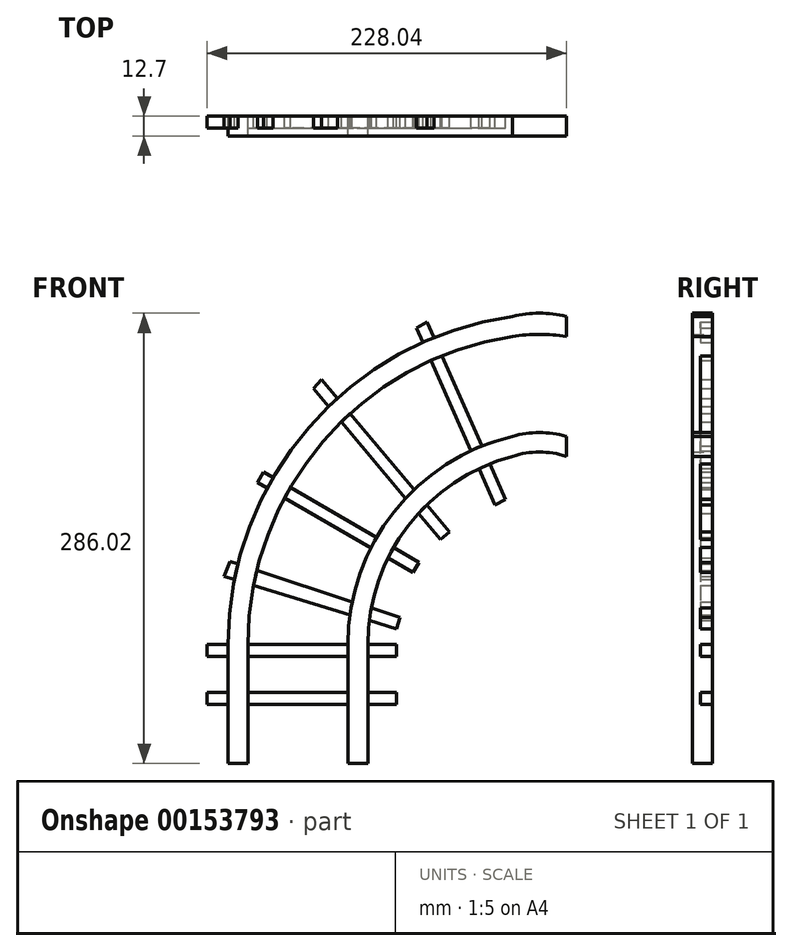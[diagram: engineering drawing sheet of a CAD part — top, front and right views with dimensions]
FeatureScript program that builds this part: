
annotation { "Feature Type Name" : "Feature", "Feature Type Description" : "" }
export const myFeature = defineFeature(function(context is Context, id is Id, definition is map)
    precondition{}
    {
        {
            var Q0;
            Q0=qCreatedBy(makeId("Front.planeOp"),FACE);
            var sketch = newSketch(context, id + "F0", { "sketchPlane" : qUnion([Q0])});
            skLineSegment(sketch, "E0", {"start": v(-58.28, 0) * mm, "end": v(-45.58, 0) * mm});
            skLineSegment(sketch, "E1", {"start": v(-45.58, 0) * mm, "end": v(-45.58, -75.5) * mm});
            skLineSegment(sketch, "E2", {"start": v(-45.58, -75.5) * mm, "end": v(-58.28, -75.5) * mm});
            skLineSegment(sketch, "E3", {"start": v(-58.28, -75.5) * mm, "end": v(-58.28, 0) * mm});
            skLineSegment(sketch, "E4", {"start": v(17.92, 0) * mm, "end": v(30.62, 0) * mm});
            skLineSegment(sketch, "E5", {"start": v(30.62, 0) * mm, "end": v(30.62, -75.5) * mm});
            skLineSegment(sketch, "E6", {"start": v(30.62, -75.5) * mm, "end": v(17.92, -75.5) * mm});
            skLineSegment(sketch, "E7", {"start": v(17.92, -75.5) * mm, "end": v(17.92, 0) * mm});
            skArc(sketch, "E8", {"start": v(122.47, 119.63) * mm, "mid": v(56.23, 75.41) * mm, "end": v(30.62, 0) * mm});
            skArc(sketch, "E9", {"start": v(122.47, 132.33) * mm, "mid": v(47.2, 84.32) * mm, "end": v(17.92, 0) * mm});
            skArc(sketch, "E10", {"start": v(122.47, 195.83) * mm, "mid": v(2.2, 129.03) * mm, "end": v(-45.58, 0) * mm});
            skArc(sketch, "E11", {"start": v(122.47, 208.53) * mm, "mid": v(-6.8, 137.98) * mm, "end": v(-58.28, 0) * mm});
            skLineSegment(sketch, "E12", {"start": v(-71.42, -30.48) * mm, "end": v(-71.42, -38.1) * mm});
            skLineSegment(sketch, "E13", {"start": v(-71.42, -38.1) * mm, "end": v(48.77, -38.1) * mm});
            skLineSegment(sketch, "E14", {"start": v(48.77, -38.1) * mm, "end": v(48.77, -30.48) * mm});
            skLineSegment(sketch, "E15", {"start": v(48.77, -30.48) * mm, "end": v(-71.42, -30.48) * mm});
            skLineSegment(sketch, "E16", {"start": v(-71.42, 0) * mm, "end": v(-71.42, -7.62) * mm});
            skLineSegment(sketch, "E17", {"start": v(-71.42, -7.62) * mm, "end": v(48.77, -7.62) * mm});
            skLineSegment(sketch, "E18", {"start": v(48.77, -7.62) * mm, "end": v(48.77, 0) * mm});
            skLineSegment(sketch, "E19", {"start": v(48.77, 0) * mm, "end": v(-71.42, 0) * mm});
            skLineSegment(sketch, "E20", {"start": v(-57.02, 52.83) * mm, "end": v(-60.61, 43.26) * mm});
            skLineSegment(sketch, "E21", {"start": v(-60.61, 43.26) * mm, "end": v(48.67, 9.97) * mm});
            skLineSegment(sketch, "E22", {"start": v(48.67, 9.97) * mm, "end": v(50.89, 17.26) * mm});
            skLineSegment(sketch, "E23", {"start": v(-57.02, 52.83) * mm, "end": v(50.89, 17.26) * mm});
            skLineSegment(sketch, "E24", {"start": v(-35.6, 109.54) * mm, "end": v(-39.43, 102.95) * mm});
            skLineSegment(sketch, "E25", {"start": v(-39.43, 102.95) * mm, "end": v(59.36, 45.68) * mm});
            skLineSegment(sketch, "E26", {"start": v(59.36, 45.68) * mm, "end": v(63.18, 52.28) * mm});
            skLineSegment(sketch, "E27", {"start": v(63.18, 52.28) * mm, "end": v(-35.6, 109.54) * mm});
            skLineSegment(sketch, "E28", {"start": v(-4.06, 162.77) * mm, "end": v(1.23, 168.25) * mm});
            skLineSegment(sketch, "E29", {"start": v(-4.06, 162.77) * mm, "end": v(76.6, 66.78) * mm});
            skLineSegment(sketch, "E30", {"start": v(76.6, 66.78) * mm, "end": v(82.43, 71.69) * mm});
            skLineSegment(sketch, "E31", {"start": v(82.43, 71.69) * mm, "end": v(1.23, 168.25) * mm});
            skLineSegment(sketch, "E32", {"start": v(61.48, 201.09) * mm, "end": v(68.05, 204.95) * mm});
            skLineSegment(sketch, "E33", {"start": v(68.05, 204.95) * mm, "end": v(118.1, 92.17) * mm});
            skLineSegment(sketch, "E34", {"start": v(61.48, 201.09) * mm, "end": v(111.28, 88.77) * mm});
            skLineSegment(sketch, "E35", {"start": v(111.28, 88.77) * mm, "end": v(118.1, 92.17) * mm});
            skArc(sketch, "E36", {"start": v(156.62, 195.83) * mm, "mid": v(139.55, 197) * mm, "end": v(122.47, 195.83) * mm});
            skArc(sketch, "E37", {"start": v(156.62, 208.53) * mm, "mid": v(139.55, 210.51) * mm, "end": v(122.47, 208.53) * mm});
            skLineSegment(sketch, "E38", {"start": v(156.62, 208.53) * mm, "end": v(156.62, 195.83) * mm});
            skArc(sketch, "E39", {"start": v(156.62, 132.33) * mm, "mid": v(139.55, 134.61) * mm, "end": v(122.47, 132.33) * mm});
            skArc(sketch, "E40", {"start": v(156.62, 119.63) * mm, "mid": v(139.55, 122.32) * mm, "end": v(122.47, 119.63) * mm});
            skLineSegment(sketch, "E41", {"start": v(156.62, 132.33) * mm, "end": v(156.62, 119.63) * mm});
            skSolve(sketch);
        }
        {
            var Q0;
            {var subQ0=sQuery(id+"F0.wireOp",EDGE,"ZuArALKP-UWyr-F3a2-eclf-R7YVd7WB1G47");Q0=makeQuery(id+"F0.imprint","IMPRINT",FACE,{"disambiguationData":[TD([[makeQuery(id+"F0.imprint","IMPRINT",EDGE,{"derivedFrom":subQ0}),-1.0]])]});}
            var Q1;
            {var subQ0=sQuery(id+"F0.wireOp",EDGE,"E33");var subQ1=sQuery(id+"F0.wireOp",EDGE,"E10");var subQ2=makeQuery(id+"F0.imprint","INTERSECT",VERTEX,{"derivedFrom":[subQ1,subQ0]});Q1=makeQuery(id+"F0.imprint","IMPRINT",FACE,{"disambiguationData":[TD([[makeQuery(id+"F0.imprint","IMPRINT",EDGE,{"disambiguationData":[TD([[subQ2,-1.0]])],"derivedFrom":subQ1}),-1.0]])]});}
            var Q2;
            {var subQ0=sQuery(id+"F0.wireOp",EDGE,"E34");var subQ1=sQuery(id+"F0.wireOp",EDGE,"E10");var subQ2=makeQuery(id+"F0.imprint","INTERSECT",VERTEX,{"derivedFrom":[subQ1,subQ0]});Q2=makeQuery(id+"F0.imprint","IMPRINT",FACE,{"disambiguationData":[TD([[makeQuery(id+"F0.imprint","IMPRINT",EDGE,{"disambiguationData":[TD([[subQ2,-1.0]])],"derivedFrom":subQ1}),-1.0]])]});}
            var Q3;
            {var subQ0=sQuery(id+"F0.wireOp",EDGE,"E31");var subQ1=sQuery(id+"F0.wireOp",EDGE,"E10");var subQ2=makeQuery(id+"F0.imprint","INTERSECT",VERTEX,{"derivedFrom":[subQ1,subQ0]});Q3=makeQuery(id+"F0.imprint","IMPRINT",FACE,{"disambiguationData":[TD([[makeQuery(id+"F0.imprint","IMPRINT",EDGE,{"disambiguationData":[TD([[subQ2,-1.0]])],"derivedFrom":subQ1}),-1.0]])]});}
            var Q4;
            {var subQ0=sQuery(id+"F0.wireOp",EDGE,"E29");var subQ1=sQuery(id+"F0.wireOp",EDGE,"E10");var subQ2=makeQuery(id+"F0.imprint","INTERSECT",VERTEX,{"derivedFrom":[subQ1,subQ0]});Q4=makeQuery(id+"F0.imprint","IMPRINT",FACE,{"disambiguationData":[TD([[makeQuery(id+"F0.imprint","IMPRINT",EDGE,{"disambiguationData":[TD([[subQ2,-1.0]])],"derivedFrom":subQ1}),-1.0]])]});}
            var Q5;
            {var subQ0=sQuery(id+"F0.wireOp",EDGE,"E25");var subQ1=sQuery(id+"F0.wireOp",EDGE,"E10");var subQ2=makeQuery(id+"F0.imprint","INTERSECT",VERTEX,{"derivedFrom":[subQ1,subQ0]});Q5=makeQuery(id+"F0.imprint","IMPRINT",FACE,{"disambiguationData":[TD([[makeQuery(id+"F0.imprint","IMPRINT",EDGE,{"disambiguationData":[TD([[subQ2,-1.0]])],"derivedFrom":subQ1}),-1.0]])]});}
            var Q6;
            {var subQ0=sQuery(id+"F0.wireOp",EDGE,"E27");var subQ1=sQuery(id+"F0.wireOp",EDGE,"E10");var subQ2=makeQuery(id+"F0.imprint","INTERSECT",VERTEX,{"derivedFrom":[subQ1,subQ0]});Q6=makeQuery(id+"F0.imprint","IMPRINT",FACE,{"disambiguationData":[TD([[makeQuery(id+"F0.imprint","IMPRINT",EDGE,{"disambiguationData":[TD([[subQ2,-1.0]])],"derivedFrom":subQ1}),-1.0]])]});}
            var Q7;
            {var subQ0=sQuery(id+"F0.wireOp",EDGE,"E23");var subQ1=sQuery(id+"F0.wireOp",EDGE,"E10");var subQ2=makeQuery(id+"F0.imprint","INTERSECT",VERTEX,{"derivedFrom":[subQ1,subQ0]});Q7=makeQuery(id+"F0.imprint","IMPRINT",FACE,{"disambiguationData":[TD([[makeQuery(id+"F0.imprint","IMPRINT",EDGE,{"disambiguationData":[TD([[subQ2,-1.0]])],"derivedFrom":subQ1}),-1.0]])]});}
            var Q8;
            {var subQ3=sQuery(id+"F0.wireOp",EDGE,"E21");var subQ5=sQuery(id+"F0.wireOp",EDGE,"E11");var subQ7=makeQuery(id+"F0.imprint","INTERSECT",VERTEX,{"derivedFrom":[subQ5,subQ3]});Q8=makeQuery(id+"F0.imprint","IMPRINT",FACE,{"disambiguationData":[TD([[makeQuery(id+"F0.imprint","IMPRINT",EDGE,{"disambiguationData":[TD([[subQ7,-1.0]])],"derivedFrom":subQ3}),-1.0]])]});}
            var Q9;
            {var subQ3=sQuery(id+"F0.wireOp",EDGE,"E17");var subQ5=sQuery(id+"F0.wireOp",EDGE,"E3");var subQ6=makeQuery(id+"F0.imprint","INTERSECT",VERTEX,{"derivedFrom":[subQ5,subQ3]});Q9=makeQuery(id+"F0.imprint","IMPRINT",FACE,{"disambiguationData":[TD([[makeQuery(id+"F0.imprint","IMPRINT",EDGE,{"disambiguationData":[TD([[subQ6,-1.0]])],"derivedFrom":subQ3}),1.0]])]});}
            var Q10;
            {var subQ0=sQuery(id+"F0.wireOp",EDGE,"E17");var subQ1=sQuery(id+"F0.wireOp",EDGE,"E1");var subQ2=makeQuery(id+"F0.imprint","INTERSECT",VERTEX,{"derivedFrom":[subQ1,subQ0]});Q10=makeQuery(id+"F0.imprint","IMPRINT",FACE,{"disambiguationData":[TD([[makeQuery(id+"F0.imprint","IMPRINT",EDGE,{"disambiguationData":[TD([[subQ2,-1.0]])],"derivedFrom":subQ1}),-1.0]])]});}
            var Q11;
            {var subQ0=sQuery(id+"F0.wireOp",EDGE,"E13");var subQ1=sQuery(id+"F0.wireOp",EDGE,"E1");var subQ2=makeQuery(id+"F0.imprint","INTERSECT",VERTEX,{"derivedFrom":[subQ1,subQ0]});Q11=makeQuery(id+"F0.imprint","IMPRINT",FACE,{"disambiguationData":[TD([[makeQuery(id+"F0.imprint","IMPRINT",EDGE,{"disambiguationData":[TD([[subQ2,1.0]])],"derivedFrom":subQ1}),-1.0]])]});}
            var Q12;
            {var subQ0=sQuery(id+"F0.wireOp",EDGE,"E2");Q12=makeQuery(id+"F0.imprint","IMPRINT",FACE,{"disambiguationData":[TD([[makeQuery(id+"F0.imprint","IMPRINT",EDGE,{"derivedFrom":subQ0}),-1.0]])]});}
            var Q13;
            {var subQ0=sQuery(id+"F0.wireOp",EDGE,"E6");Q13=makeQuery(id+"F0.imprint","IMPRINT",FACE,{"disambiguationData":[TD([[makeQuery(id+"F0.imprint","IMPRINT",EDGE,{"derivedFrom":subQ0}),-1.0]])]});}
            var Q14;
            {var subQ0=sQuery(id+"F0.wireOp",EDGE,"E15");var subQ1=sQuery(id+"F0.wireOp",EDGE,"E5");var subQ2=makeQuery(id+"F0.imprint","INTERSECT",VERTEX,{"derivedFrom":[subQ1,subQ0]});Q14=makeQuery(id+"F0.imprint","IMPRINT",FACE,{"disambiguationData":[TD([[makeQuery(id+"F0.imprint","IMPRINT",EDGE,{"disambiguationData":[TD([[subQ2,-1.0]])],"derivedFrom":subQ1}),-1.0]])]});}
            var Q15;
            {var subQ0=sQuery(id+"F0.wireOp",EDGE,"E17");var subQ1=sQuery(id+"F0.wireOp",EDGE,"E5");var subQ2=makeQuery(id+"F0.imprint","INTERSECT",VERTEX,{"derivedFrom":[subQ1,subQ0]});Q15=makeQuery(id+"F0.imprint","IMPRINT",FACE,{"disambiguationData":[TD([[makeQuery(id+"F0.imprint","IMPRINT",EDGE,{"disambiguationData":[TD([[subQ2,-1.0]])],"derivedFrom":subQ1}),-1.0]])]});}
            var Q16;
            {var subQ1=sQuery(id+"F0.wireOp",EDGE,"E5");var subQ3=sQuery(id+"F0.wireOp",EDGE,"E17");var subQ4=makeQuery(id+"F0.imprint","INTERSECT",VERTEX,{"derivedFrom":[subQ1,subQ3]});Q16=makeQuery(id+"F0.imprint","IMPRINT",FACE,{"disambiguationData":[TD([[makeQuery(id+"F0.imprint","IMPRINT",EDGE,{"disambiguationData":[TD([[subQ4,1.0]])],"derivedFrom":subQ3}),1.0]])]});}
            var Q17;
            {var subQ1=sQuery(id+"F0.wireOp",EDGE,"E8");var subQ3=sQuery(id+"F0.wireOp",EDGE,"E21");var subQ4=makeQuery(id+"F0.imprint","INTERSECT",VERTEX,{"derivedFrom":[subQ1,subQ3]});Q17=makeQuery(id+"F0.imprint","IMPRINT",FACE,{"disambiguationData":[TD([[makeQuery(id+"F0.imprint","IMPRINT",EDGE,{"disambiguationData":[TD([[subQ4,1.0]])],"derivedFrom":subQ3}),-1.0]])]});}
            var Q18;
            {var subQ0=sQuery(id+"F0.wireOp",EDGE,"E23");var subQ1=sQuery(id+"F0.wireOp",EDGE,"E8");var subQ2=makeQuery(id+"F0.imprint","INTERSECT",VERTEX,{"derivedFrom":[subQ1,subQ0]});Q18=makeQuery(id+"F0.imprint","IMPRINT",FACE,{"disambiguationData":[TD([[makeQuery(id+"F0.imprint","IMPRINT",EDGE,{"disambiguationData":[TD([[subQ2,-1.0]])],"derivedFrom":subQ1}),-1.0]])]});}
            var Q19;
            {var subQ0=sQuery(id+"F0.wireOp",EDGE,"E25");var subQ1=sQuery(id+"F0.wireOp",EDGE,"E8");var subQ2=makeQuery(id+"F0.imprint","INTERSECT",VERTEX,{"derivedFrom":[subQ1,subQ0]});Q19=makeQuery(id+"F0.imprint","IMPRINT",FACE,{"disambiguationData":[TD([[makeQuery(id+"F0.imprint","IMPRINT",EDGE,{"disambiguationData":[TD([[subQ2,-1.0]])],"derivedFrom":subQ1}),-1.0]])]});}
            var Q20;
            {var subQ0=sQuery(id+"F0.wireOp",EDGE,"E27");var subQ1=sQuery(id+"F0.wireOp",EDGE,"E8");var subQ2=makeQuery(id+"F0.imprint","INTERSECT",VERTEX,{"derivedFrom":[subQ1,subQ0]});Q20=makeQuery(id+"F0.imprint","IMPRINT",FACE,{"disambiguationData":[TD([[makeQuery(id+"F0.imprint","IMPRINT",EDGE,{"disambiguationData":[TD([[subQ2,-1.0]])],"derivedFrom":subQ1}),-1.0]])]});}
            var Q21;
            {var subQ0=sQuery(id+"F0.wireOp",EDGE,"E29");var subQ1=sQuery(id+"F0.wireOp",EDGE,"E8");var subQ2=makeQuery(id+"F0.imprint","INTERSECT",VERTEX,{"derivedFrom":[subQ1,subQ0]});Q21=makeQuery(id+"F0.imprint","IMPRINT",FACE,{"disambiguationData":[TD([[makeQuery(id+"F0.imprint","IMPRINT",EDGE,{"disambiguationData":[TD([[subQ2,-1.0]])],"derivedFrom":subQ1}),-1.0]])]});}
            var Q22;
            {var subQ0=sQuery(id+"F0.wireOp",EDGE,"E31");var subQ1=sQuery(id+"F0.wireOp",EDGE,"E8");var subQ2=makeQuery(id+"F0.imprint","INTERSECT",VERTEX,{"derivedFrom":[subQ1,subQ0]});Q22=makeQuery(id+"F0.imprint","IMPRINT",FACE,{"disambiguationData":[TD([[makeQuery(id+"F0.imprint","IMPRINT",EDGE,{"disambiguationData":[TD([[subQ2,-1.0]])],"derivedFrom":subQ1}),-1.0]])]});}
            var Q23;
            {var subQ0=sQuery(id+"F0.wireOp",EDGE,"E34");var subQ1=sQuery(id+"F0.wireOp",EDGE,"E8");var subQ2=makeQuery(id+"F0.imprint","INTERSECT",VERTEX,{"derivedFrom":[subQ1,subQ0]});Q23=makeQuery(id+"F0.imprint","IMPRINT",FACE,{"disambiguationData":[TD([[makeQuery(id+"F0.imprint","IMPRINT",EDGE,{"disambiguationData":[TD([[subQ2,-1.0]])],"derivedFrom":subQ1}),-1.0]])]});}
            var Q24;
            {var subQ0=sQuery(id+"F0.wireOp",EDGE,"E33");var subQ1=sQuery(id+"F0.wireOp",EDGE,"E8");var subQ2=makeQuery(id+"F0.imprint","INTERSECT",VERTEX,{"derivedFrom":[subQ1,subQ0]});Q24=makeQuery(id+"F0.imprint","IMPRINT",FACE,{"disambiguationData":[TD([[makeQuery(id+"F0.imprint","IMPRINT",EDGE,{"disambiguationData":[TD([[subQ2,-1.0]])],"derivedFrom":subQ1}),-1.0]])]});}
            var Q25;
            {var subQ0=sQuery(id+"F0.wireOp",EDGE,"iaoba4zp-OYrk-QPT7-W3qE-r9RfF5j1HngC");Q25=makeQuery(id+"F0.imprint","IMPRINT",FACE,{"disambiguationData":[TD([[makeQuery(id+"F0.imprint","IMPRINT",EDGE,{"derivedFrom":subQ0}),-1.0]])]});}
            var Q26;
            {var subQ0=sQuery(id+"F0.wireOp",EDGE,"E36");Q26=makeQuery(id+"F0.imprint","IMPRINT",FACE,{"disambiguationData":[TD([[makeQuery(id+"F0.imprint","IMPRINT",EDGE,{"derivedFrom":subQ0}),-1.0]])]});}
            var Q27;
            {var subQ5=sQuery(id+"F0.wireOp",EDGE,"E39");Q27=makeQuery(id+"F0.imprint","IMPRINT",FACE,{"disambiguationData":[TD([[makeQuery(id+"F0.imprint","IMPRINT",EDGE,{"derivedFrom":subQ5}),1.0]])]});}
            extrude(context, id + "F1", {"entities" : qUnion([Q0, Q1, Q2, Q3, Q4, Q5, Q6, Q7, Q8, Q9, Q10, Q11, Q12, Q13, Q14, Q15, Q16, Q17, Q18, Q19, Q20, Q21, Q22, Q23, Q24, Q25, Q26, Q27]), "depth" : 12.7 * mm});
        }
        {
            var Q0;
            {var subQ0=sQuery(id+"F0.wireOp",EDGE,"E33");var subQ1=sQuery(id+"F0.wireOp",EDGE,"E9");var subQ2=makeQuery(id+"F0.imprint","INTERSECT",VERTEX,{"derivedFrom":[subQ1,subQ0]});Q0=makeQuery(id+"F0.imprint","IMPRINT",FACE,{"disambiguationData":[TD([[makeQuery(id+"F0.imprint","IMPRINT",EDGE,{"disambiguationData":[TD([[subQ2,-1.0]])],"derivedFrom":subQ1}),-1.0]])]});}
            var Q1;
            {var subQ0=sQuery(id+"F0.wireOp",EDGE,"E31");var subQ1=sQuery(id+"F0.wireOp",EDGE,"E9");var subQ2=makeQuery(id+"F0.imprint","INTERSECT",VERTEX,{"derivedFrom":[subQ1,subQ0]});Q1=makeQuery(id+"F0.imprint","IMPRINT",FACE,{"disambiguationData":[TD([[makeQuery(id+"F0.imprint","IMPRINT",EDGE,{"disambiguationData":[TD([[subQ2,-1.0]])],"derivedFrom":subQ1}),-1.0]])]});}
            var Q2;
            {var subQ0=sQuery(id+"F0.wireOp",EDGE,"E27");var subQ1=sQuery(id+"F0.wireOp",EDGE,"E9");var subQ2=makeQuery(id+"F0.imprint","INTERSECT",VERTEX,{"derivedFrom":[subQ1,subQ0]});Q2=makeQuery(id+"F0.imprint","IMPRINT",FACE,{"disambiguationData":[TD([[makeQuery(id+"F0.imprint","IMPRINT",EDGE,{"disambiguationData":[TD([[subQ2,-1.0]])],"derivedFrom":subQ1}),-1.0]])]});}
            var Q3;
            {var subQ0=sQuery(id+"F0.wireOp",EDGE,"E23");var subQ1=sQuery(id+"F0.wireOp",EDGE,"E9");var subQ2=makeQuery(id+"F0.imprint","INTERSECT",VERTEX,{"derivedFrom":[subQ1,subQ0]});Q3=makeQuery(id+"F0.imprint","IMPRINT",FACE,{"disambiguationData":[TD([[makeQuery(id+"F0.imprint","IMPRINT",EDGE,{"disambiguationData":[TD([[subQ2,-1.0]])],"derivedFrom":subQ1}),-1.0]])]});}
            var Q4;
            {var subQ1=sQuery(id+"F0.wireOp",EDGE,"E1");var subQ3=sQuery(id+"F0.wireOp",EDGE,"E17");var subQ4=makeQuery(id+"F0.imprint","INTERSECT",VERTEX,{"derivedFrom":[subQ1,subQ3]});Q4=makeQuery(id+"F0.imprint","IMPRINT",FACE,{"disambiguationData":[TD([[makeQuery(id+"F0.imprint","IMPRINT",EDGE,{"disambiguationData":[TD([[subQ4,-1.0]])],"derivedFrom":subQ3}),1.0]])]});}
            var Q5;
            {var subQ0=sQuery(id+"F0.wireOp",EDGE,"E13");var subQ1=sQuery(id+"F0.wireOp",EDGE,"E1");var subQ2=makeQuery(id+"F0.imprint","INTERSECT",VERTEX,{"derivedFrom":[subQ1,subQ0]});Q5=makeQuery(id+"F0.imprint","IMPRINT",FACE,{"disambiguationData":[TD([[makeQuery(id+"F0.imprint","IMPRINT",EDGE,{"disambiguationData":[TD([[subQ2,1.0]])],"derivedFrom":subQ1}),1.0]])]});}
            var Q6;
            {var subQ5=sQuery(id+"F0.wireOp",EDGE,"E14");Q6=makeQuery(id+"F0.imprint","IMPRINT",FACE,{"disambiguationData":[TD([[makeQuery(id+"F0.imprint","IMPRINT",EDGE,{"derivedFrom":subQ5}),1.0]])]});}
            var Q7;
            {var subQ5=sQuery(id+"F0.wireOp",EDGE,"E18");Q7=makeQuery(id+"F0.imprint","IMPRINT",FACE,{"disambiguationData":[TD([[makeQuery(id+"F0.imprint","IMPRINT",EDGE,{"derivedFrom":subQ5}),1.0]])]});}
            var Q8;
            {var subQ5=sQuery(id+"F0.wireOp",EDGE,"E22");Q8=makeQuery(id+"F0.imprint","IMPRINT",FACE,{"disambiguationData":[TD([[makeQuery(id+"F0.imprint","IMPRINT",EDGE,{"derivedFrom":subQ5}),1.0]])]});}
            var Q9;
            {var subQ5=sQuery(id+"F0.wireOp",EDGE,"E26");Q9=makeQuery(id+"F0.imprint","IMPRINT",FACE,{"disambiguationData":[TD([[makeQuery(id+"F0.imprint","IMPRINT",EDGE,{"derivedFrom":subQ5}),1.0]])]});}
            var Q10;
            {var subQ5=sQuery(id+"F0.wireOp",EDGE,"E30");Q10=makeQuery(id+"F0.imprint","IMPRINT",FACE,{"disambiguationData":[TD([[makeQuery(id+"F0.imprint","IMPRINT",EDGE,{"derivedFrom":subQ5}),1.0]])]});}
            var Q11;
            {var subQ5=sQuery(id+"F0.wireOp",EDGE,"E35");Q11=makeQuery(id+"F0.imprint","IMPRINT",FACE,{"disambiguationData":[TD([[makeQuery(id+"F0.imprint","IMPRINT",EDGE,{"derivedFrom":subQ5}),1.0]])]});}
            var Q12;
            {var subQ5=sQuery(id+"F0.wireOp",EDGE,"E32");Q12=makeQuery(id+"F0.imprint","IMPRINT",FACE,{"disambiguationData":[TD([[makeQuery(id+"F0.imprint","IMPRINT",EDGE,{"derivedFrom":subQ5}),-1.0]])]});}
            var Q13;
            {var subQ5=sQuery(id+"F0.wireOp",EDGE,"E28");Q13=makeQuery(id+"F0.imprint","IMPRINT",FACE,{"disambiguationData":[TD([[makeQuery(id+"F0.imprint","IMPRINT",EDGE,{"derivedFrom":subQ5}),-1.0]])]});}
            var Q14;
            {var subQ5=sQuery(id+"F0.wireOp",EDGE,"E24");Q14=makeQuery(id+"F0.imprint","IMPRINT",FACE,{"disambiguationData":[TD([[makeQuery(id+"F0.imprint","IMPRINT",EDGE,{"derivedFrom":subQ5}),1.0]])]});}
            var Q15;
            {var subQ5=sQuery(id+"F0.wireOp",EDGE,"E20");Q15=makeQuery(id+"F0.imprint","IMPRINT",FACE,{"disambiguationData":[TD([[makeQuery(id+"F0.imprint","IMPRINT",EDGE,{"derivedFrom":subQ5}),1.0]])]});}
            var Q16;
            {var subQ5=sQuery(id+"F0.wireOp",EDGE,"E16");Q16=makeQuery(id+"F0.imprint","IMPRINT",FACE,{"disambiguationData":[TD([[makeQuery(id+"F0.imprint","IMPRINT",EDGE,{"derivedFrom":subQ5}),1.0]])]});}
            var Q17;
            {var subQ5=sQuery(id+"F0.wireOp",EDGE,"E12");Q17=makeQuery(id+"F0.imprint","IMPRINT",FACE,{"disambiguationData":[TD([[makeQuery(id+"F0.imprint","IMPRINT",EDGE,{"derivedFrom":subQ5}),1.0]])]});}
            extrude(context, id + "F2", {"entities" : qUnion([Q0, Q1, Q2, Q3, Q4, Q5, Q6, Q7, Q8, Q9, Q10, Q11, Q12, Q13, Q14, Q15, Q16, Q17]), "depth" : 7.62 * mm});
        }
    });
